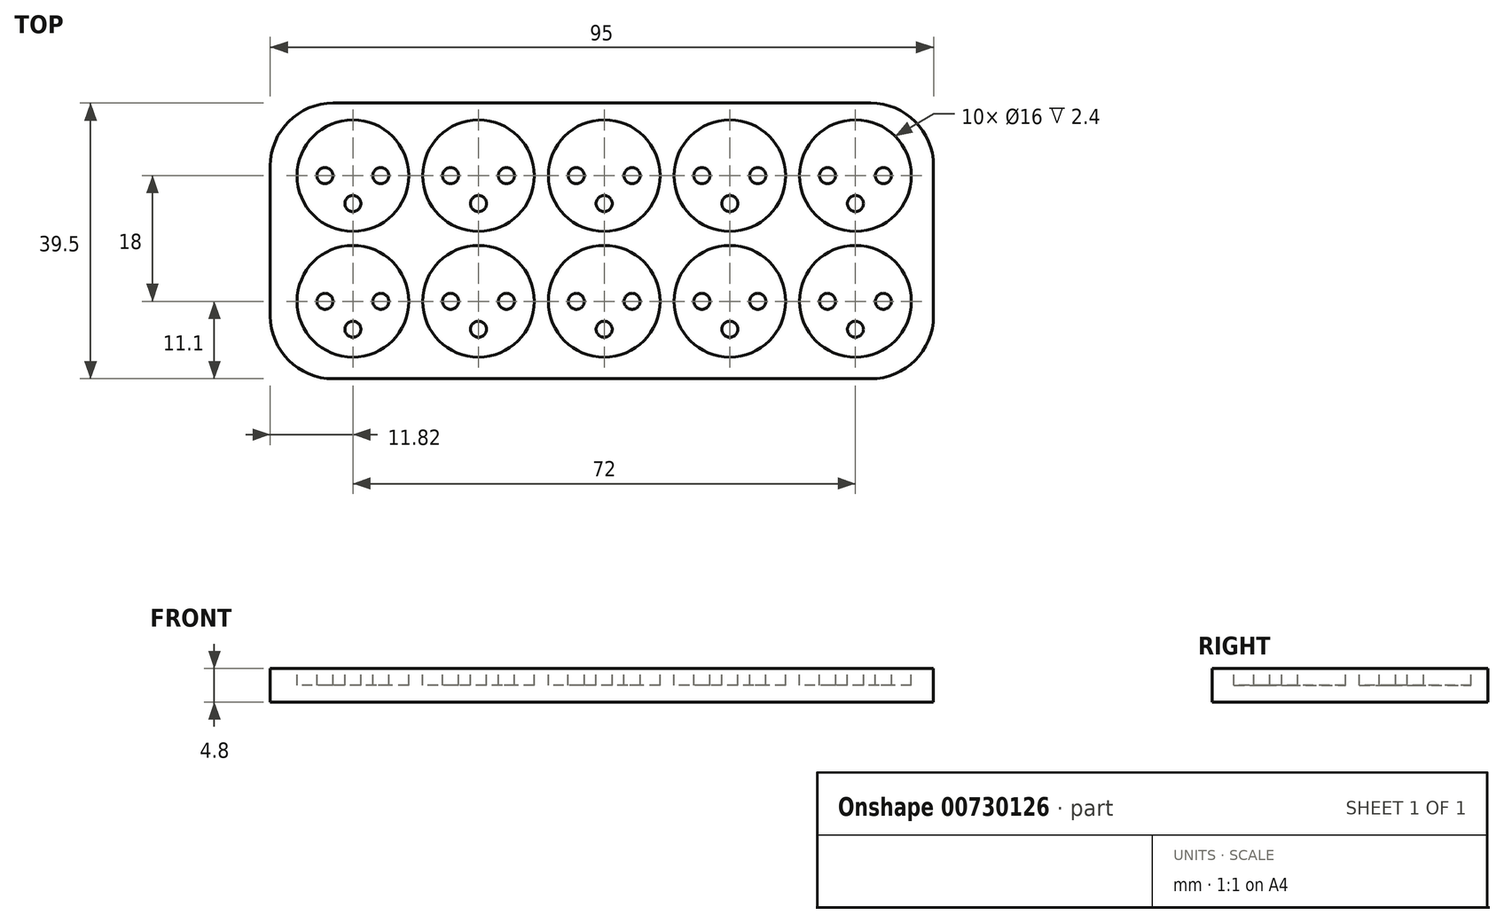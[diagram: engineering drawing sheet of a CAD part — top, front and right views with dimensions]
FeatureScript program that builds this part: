
annotation { "Feature Type Name" : "Feature", "Feature Type Description" : "" }
export const myFeature = defineFeature(function(context is Context, id is Id, definition is map)
    precondition{}
    {
        {
            var Q0;
            Q0=qCreatedBy(makeId("Top.planeOp"),FACE);
            var sketch = newSketch(context, id + "F0", { "sketchPlane" : qUnion([Q0])});
            skLineSegment(sketch, "E0.bottom", {"start": v(-11.82, 28.4) * mm, "end": v(83.18, 28.4) * mm});
            skLineSegment(sketch, "E0.top", {"start": v(-11.82, -11.1) * mm, "end": v(83.18, -11.1) * mm});
            skLineSegment(sketch, "E0.left", {"start": v(-11.82, 28.4) * mm, "end": v(-11.82, -11.1) * mm});
            skLineSegment(sketch, "E0.right", {"start": v(83.18, 28.4) * mm, "end": v(83.18, -11.1) * mm});
            skSolve(sketch);
        }
        {
            var Q0;
            Q0=makeQuery(id+"F0.imprint","IMPRINT",FACE,{"disambiguationData":[TD([[makeQuery(id+"F0.imprint","IMPRINT",EDGE,{"derivedFrom":sQuery(id+"F0.wireOp",EDGE,"E0.bottom")}),-1.0]])]});
            extrude(context, id + "F1", {"entities" : qUnion([Q0]), "depth" : 4.8 * mm, "offsetDistance" : 25 * mm});
        }
        {
            var Q0;
            Q0=makeQuery(id+"F1.opExtrude","CAP_FACE",FACE,{"disambiguationData":[OSD([sQuery(id+"F0.wireOp",EDGE,"E0.bottom"),sQuery(id+"F0.wireOp",EDGE,"E0.top"),sQuery(id+"F0.wireOp",EDGE,"E0.left"),sQuery(id+"F0.wireOp",EDGE,"E0.right")])],"isStart":false});
            var sketch = newSketch(context, id + "F2", { "sketchPlane" : qUnion([Q0])});
            skCircle(sketch, "E1", {"center": v(0, 0) * mm, "radius": 8 * mm});
            skLineSegment(sketch, "E2", {"start": v(-8, 0) * mm, "end": v(8, 0) * mm, "construction": true});
            skLineSegment(sketch, "E3", {"start": v(0, 8) * mm, "end": v(0, -8) * mm, "construction": true});
            skCircle(sketch, "E4", {"center": v(-4, 0) * mm, "radius": 1.15 * mm});
            skCircle(sketch, "E5", {"center": v(4, 0) * mm, "radius": 1.15 * mm});
            skCircle(sketch, "E6", {"center": v(0, -4) * mm, "radius": 1.15 * mm});
            skCircle(sketch, "E7.0.1.0", {"center": v(0, 18) * mm, "radius": 8 * mm});
            skCircle(sketch, "E7.0.1.1", {"center": v(4, 18) * mm, "radius": 1.15 * mm});
            skCircle(sketch, "E7.0.1.2", {"center": v(0, 14) * mm, "radius": 1.15 * mm});
            skCircle(sketch, "E7.0.1.3", {"center": v(-4, 18) * mm, "radius": 1.15 * mm});
            skCircle(sketch, "E7.1.0.0", {"center": v(18, 0) * mm, "radius": 8 * mm});
            skCircle(sketch, "E7.1.0.1", {"center": v(22, 0) * mm, "radius": 1.15 * mm});
            skCircle(sketch, "E7.1.0.2", {"center": v(18, -4) * mm, "radius": 1.15 * mm});
            skCircle(sketch, "E7.1.0.3", {"center": v(14, 0) * mm, "radius": 1.15 * mm});
            skCircle(sketch, "E7.1.1.0", {"center": v(18, 18) * mm, "radius": 8 * mm});
            skCircle(sketch, "E7.1.1.1", {"center": v(22, 18) * mm, "radius": 1.15 * mm});
            skCircle(sketch, "E7.1.1.2", {"center": v(18, 14) * mm, "radius": 1.15 * mm});
            skCircle(sketch, "E7.1.1.3", {"center": v(14, 18) * mm, "radius": 1.15 * mm});
            skCircle(sketch, "E7.2.0.0", {"center": v(36, 0) * mm, "radius": 8 * mm});
            skCircle(sketch, "E7.2.0.1", {"center": v(40, 0) * mm, "radius": 1.15 * mm});
            skCircle(sketch, "E7.2.0.2", {"center": v(36, -4) * mm, "radius": 1.15 * mm});
            skCircle(sketch, "E7.2.0.3", {"center": v(32, 0) * mm, "radius": 1.15 * mm});
            skCircle(sketch, "E7.2.1.0", {"center": v(36, 18) * mm, "radius": 8 * mm});
            skCircle(sketch, "E7.2.1.1", {"center": v(40, 18) * mm, "radius": 1.15 * mm});
            skCircle(sketch, "E7.2.1.2", {"center": v(36, 14) * mm, "radius": 1.15 * mm});
            skCircle(sketch, "E7.2.1.3", {"center": v(32, 18) * mm, "radius": 1.15 * mm});
            skCircle(sketch, "E7.3.0.0", {"center": v(54, 0) * mm, "radius": 8 * mm});
            skCircle(sketch, "E7.3.0.1", {"center": v(58, 0) * mm, "radius": 1.15 * mm});
            skCircle(sketch, "E7.3.0.2", {"center": v(54, -4) * mm, "radius": 1.15 * mm});
            skCircle(sketch, "E7.3.0.3", {"center": v(50, 0) * mm, "radius": 1.15 * mm});
            skCircle(sketch, "E7.3.1.0", {"center": v(54, 18) * mm, "radius": 8 * mm});
            skCircle(sketch, "E7.3.1.1", {"center": v(58, 18) * mm, "radius": 1.15 * mm});
            skCircle(sketch, "E7.3.1.2", {"center": v(54, 14) * mm, "radius": 1.15 * mm});
            skCircle(sketch, "E7.3.1.3", {"center": v(50, 18) * mm, "radius": 1.15 * mm});
            skCircle(sketch, "E7.4.0.0", {"center": v(72, 0) * mm, "radius": 8 * mm});
            skCircle(sketch, "E7.4.0.1", {"center": v(76, 0) * mm, "radius": 1.15 * mm});
            skCircle(sketch, "E7.4.0.2", {"center": v(72, -4) * mm, "radius": 1.15 * mm});
            skCircle(sketch, "E7.4.0.3", {"center": v(68, 0) * mm, "radius": 1.15 * mm});
            skCircle(sketch, "E7.4.1.0", {"center": v(72, 18) * mm, "radius": 8 * mm});
            skCircle(sketch, "E7.4.1.1", {"center": v(76, 18) * mm, "radius": 1.15 * mm});
            skCircle(sketch, "E7.4.1.2", {"center": v(72, 14) * mm, "radius": 1.15 * mm});
            skCircle(sketch, "E7.4.1.3", {"center": v(68, 18) * mm, "radius": 1.15 * mm});
            skLineSegment(sketch, "E7.direction1", {"start": v(0, 0) * mm, "end": v(18, 0) * mm, "construction": true});
            skLineSegment(sketch, "E7.direction2", {"start": v(0, 0) * mm, "end": v(0, 18) * mm, "construction": true});
            skSolve(sketch);
        }
        {
            var Q0;
            Q0=makeQuery(id+"F2.imprint","IMPRINT",FACE,{"disambiguationData":[TD([[makeQuery(id+"F2.imprint","IMPRINT",EDGE,{"derivedFrom":sQuery(id+"F2.wireOp",EDGE,"E7.0.1.0")}),1.0]])]});
            var Q1;
            Q1=makeQuery(id+"F2.imprint","IMPRINT",FACE,{"disambiguationData":[TD([[makeQuery(id+"F2.imprint","IMPRINT",EDGE,{"derivedFrom":sQuery(id+"F2.wireOp",EDGE,"E7.1.1.0")}),1.0]])]});
            var Q2;
            Q2=makeQuery(id+"F2.imprint","IMPRINT",FACE,{"disambiguationData":[TD([[makeQuery(id+"F2.imprint","IMPRINT",EDGE,{"derivedFrom":sQuery(id+"F2.wireOp",EDGE,"E7.2.1.0")}),1.0]])]});
            var Q3;
            Q3=makeQuery(id+"F2.imprint","IMPRINT",FACE,{"disambiguationData":[TD([[makeQuery(id+"F2.imprint","IMPRINT",EDGE,{"derivedFrom":sQuery(id+"F2.wireOp",EDGE,"E7.3.1.0")}),1.0]])]});
            var Q4;
            Q4=makeQuery(id+"F2.imprint","IMPRINT",FACE,{"disambiguationData":[TD([[makeQuery(id+"F2.imprint","IMPRINT",EDGE,{"derivedFrom":sQuery(id+"F2.wireOp",EDGE,"E7.4.1.0")}),1.0]])]});
            var Q5;
            Q5=makeQuery(id+"F2.imprint","IMPRINT",FACE,{"disambiguationData":[TD([[makeQuery(id+"F2.imprint","IMPRINT",EDGE,{"derivedFrom":sQuery(id+"F2.wireOp",EDGE,"E7.4.0.0")}),1.0]])]});
            var Q6;
            Q6=makeQuery(id+"F2.imprint","IMPRINT",FACE,{"disambiguationData":[TD([[makeQuery(id+"F2.imprint","IMPRINT",EDGE,{"derivedFrom":sQuery(id+"F2.wireOp",EDGE,"E7.3.0.0")}),1.0]])]});
            var Q7;
            Q7=makeQuery(id+"F2.imprint","IMPRINT",FACE,{"disambiguationData":[TD([[makeQuery(id+"F2.imprint","IMPRINT",EDGE,{"derivedFrom":sQuery(id+"F2.wireOp",EDGE,"E7.2.0.0")}),1.0]])]});
            var Q8;
            Q8=makeQuery(id+"F2.imprint","IMPRINT",FACE,{"disambiguationData":[TD([[makeQuery(id+"F2.imprint","IMPRINT",EDGE,{"derivedFrom":sQuery(id+"F2.wireOp",EDGE,"E7.1.0.0")}),1.0]])]});
            var Q9;
            Q9=makeQuery(id+"F2.imprint","IMPRINT",FACE,{"disambiguationData":[TD([[makeQuery(id+"F2.imprint","IMPRINT",EDGE,{"derivedFrom":sQuery(id+"F2.wireOp",EDGE,"E1")}),1.0]])]});
            extrude(context, id + "F3", {"entities" : qUnion([Q0, Q1, Q2, Q3, Q4, Q5, Q6, Q7, Q8, Q9]), "operationType" : NewBodyOperationType.REMOVE, "oppositeDirection" : true, "depth" : 2.4 * mm, "offsetDistance" : 25 * mm});
        }
        {
            var Q0;
            Q0=makeQuery(id+"F1.opExtrude","SWEPT_EDGE",EDGE,{"disambiguationData":[OSD([sQuery(id+"F0.wireOp",EDGE,"E0.top"),sQuery(id+"F0.wireOp",EDGE,"E0.left")])]});
            var Q1;
            Q1=makeQuery(id+"F1.opExtrude","SWEPT_EDGE",EDGE,{"disambiguationData":[OSD([sQuery(id+"F0.wireOp",EDGE,"E0.bottom"),sQuery(id+"F0.wireOp",EDGE,"E0.left")])]});
            var Q2;
            Q2=makeQuery(id+"F1.opExtrude","SWEPT_EDGE",EDGE,{"disambiguationData":[OSD([sQuery(id+"F0.wireOp",EDGE,"E0.top"),sQuery(id+"F0.wireOp",EDGE,"E0.right")])]});
            var Q3;
            Q3=makeQuery(id+"F1.opExtrude","SWEPT_EDGE",EDGE,{"disambiguationData":[OSD([sQuery(id+"F0.wireOp",EDGE,"E0.bottom"),sQuery(id+"F0.wireOp",EDGE,"E0.right")])]});
            fillet(context, id + "F4", {"entities" : qUnion([Q0, Q1, Q2, Q3]), "radius" : 9 * mm, "tangentPropagation" : true, "allowEdgeOverflow" : false});
        }
    });
